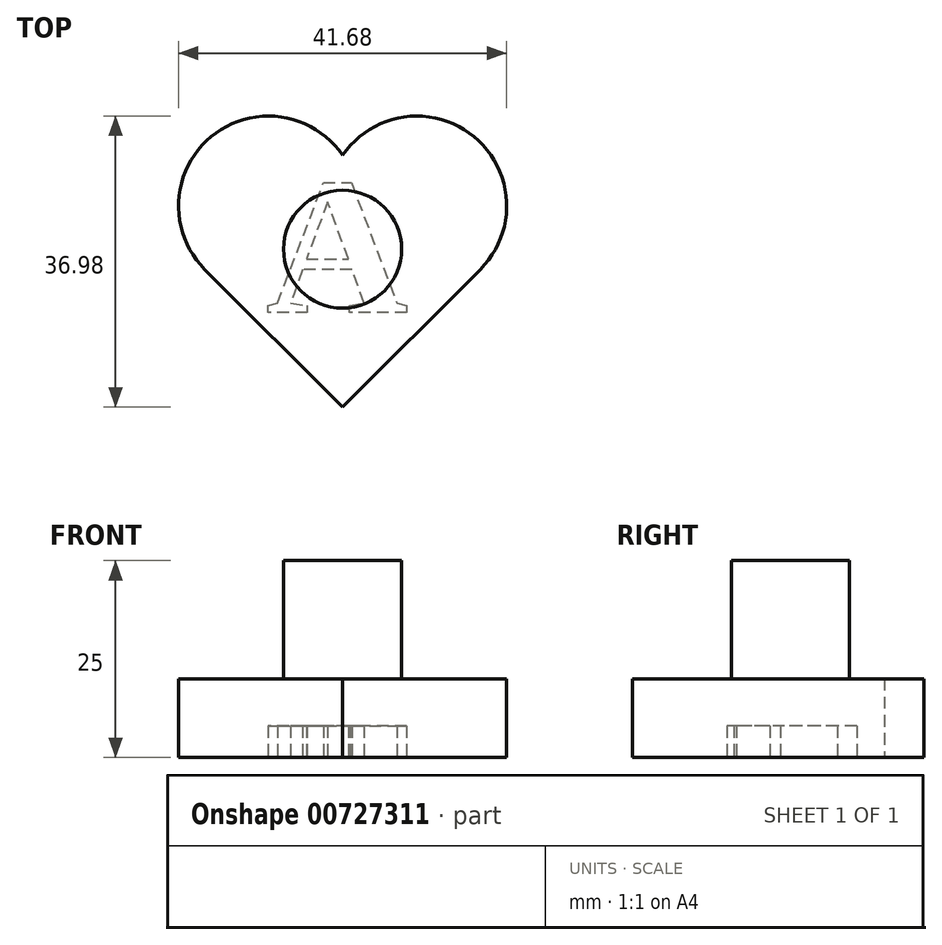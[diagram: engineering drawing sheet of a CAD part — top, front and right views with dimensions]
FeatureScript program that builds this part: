
annotation { "Feature Type Name" : "Feature", "Feature Type Description" : "" }
export const myFeature = defineFeature(function(context is Context, id is Id, definition is map)
    precondition{}
    {
        {
            var Q0;
            Q0=qCreatedBy(makeId("Top.planeOp"),FACE);
            var sketch = newSketch(context, id + "F0", { "sketchPlane" : qUnion([Q0])});
            skLineSegment(sketch, "E0", {"start": v(0, 0) * mm, "end": v(0, 32) * mm, "construction": true});
            skLineSegment(sketch, "E1", {"start": v(0, 0) * mm, "end": v(-17.5, 17.5) * mm});
            skArc(sketch, "E2", {"start": v(0, 32) * mm, "mid": v(-16.71, 34.36) * mm, "end": v(-17.5, 17.5) * mm});
            skArc(sketch, "E3.MirrorCS", {"start": v(0, 32) * mm, "mid": v(16.71, 34.36) * mm, "end": v(17.5, 17.5) * mm});
            skLineSegment(sketch, "E4.MirrorCS", {"start": v(0, 0) * mm, "end": v(17.5, 17.5) * mm});
            skSolve(sketch);
        }
        {
            var Q0;
            Q0=makeQuery(id+"F0.imprint","IMPRINT",FACE,{"disambiguationData":[TD([[makeQuery(id+"F0.imprint","IMPRINT",EDGE,{"derivedFrom":sQuery(id+"F0.wireOp",EDGE,"E1")}),-1.0]])]});
            extrude(context, id + "F1", {"entities" : qUnion([Q0]), "depth" : 10 * mm, "offsetDistance" : 25 * mm});
        }
        {
            var Q0;
            Q0=makeQuery(id+"F1.opExtrude","CAP_FACE",FACE,{"disambiguationData":[OSD([sQuery(id+"F0.wireOp",EDGE,"E1"),sQuery(id+"F0.wireOp",EDGE,"E2"),sQuery(id+"F0.wireOp",EDGE,"E3.MirrorCS"),sQuery(id+"F0.wireOp",EDGE,"E4.MirrorCS")])],"isStart":false});
            var sketch = newSketch(context, id + "F2", { "sketchPlane" : qUnion([Q0])});
            skCircle(sketch, "E5", {"center": v(0, 20.06) * mm, "radius": 7.5 * mm});
            skSolve(sketch);
        }
        {
            var Q0;
            Q0=makeQuery(id+"F2.imprint","IMPRINT",FACE,{"disambiguationData":[TD([[makeQuery(id+"F2.imprint","IMPRINT",EDGE,{"derivedFrom":sQuery(id+"F2.wireOp",EDGE,"E5")}),1.0]])]});
            extrude(context, id + "F3", {"entities" : qUnion([Q0]), "operationType" : NewBodyOperationType.ADD, "depth" : 15 * mm, "offsetDistance" : 25 * mm});
        }
        {
            var Q0;
            Q0=qCreatedBy(makeId("Top.planeOp"),FACE);
            var sketch = newSketch(context, id + "F4", { "sketchPlane" : qUnion([Q0])});
            skText(sketch, "E6", { "text": "A", "fontName": "Tinos-Bold.ttf"});
            const initialGuessF4  = {"E6": [-0.00972, 0.012, 1, 0, 0.018]};
            skSetInitialGuess(sketch, initialGuessF4);
            skSolve(sketch);
        }
        {
            var Q0;
            Q0=makeQuery(id+"F4.imprint","IMPRINT",FACE,{"disambiguationData":[TD([[makeQuery(id+"F4.imprint","IMPRINT",EDGE,{"derivedFrom":sQuery(id+"F4.wireOp",EDGE,"E6.sketch_text.stroke-0")}),-1.0]])]});
            extrude(context, id + "F5", {"entities" : qUnion([Q0]), "operationType" : NewBodyOperationType.REMOVE, "depth" : 4 * mm, "offsetDistance" : 25 * mm});
        }
    });
